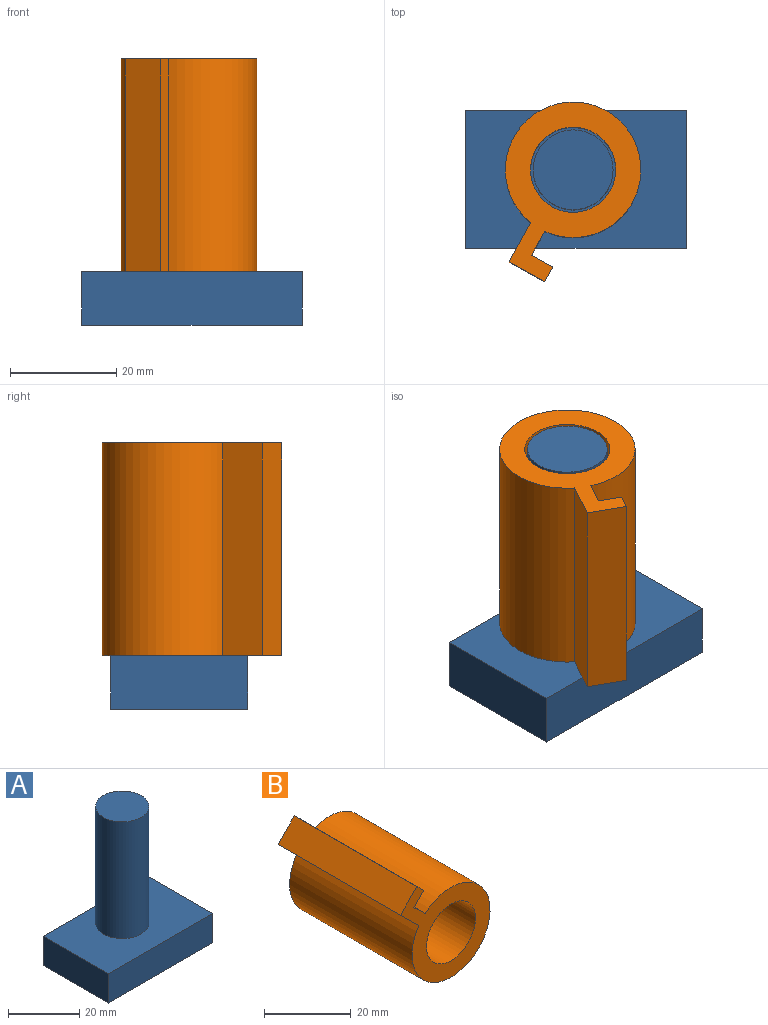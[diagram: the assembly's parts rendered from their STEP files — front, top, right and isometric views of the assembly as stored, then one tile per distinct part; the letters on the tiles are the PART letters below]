
ASSEMBLY  parts=2 mates=1
PART A: 8 faces, bbox 41.4x25.8x50 mm
  f0: cylinder r=7.5mm len=40mm, axis (0,0,-1), area 1885mm2, adj f1,f6
  f1: plane 15x15mm, normal (0,0,1), area 176.7mm2, adj f0
  f2: plane 41.36x10mm, normal (0,1,0), area 413.6mm2, adj f3,f5,f6,f7
  f3: plane 25.79x10mm, normal (-1,0,0), area 257.8mm2, adj f2,f4,f6,f7
  f4: plane 41.36x10mm, normal (0,-1,0), area 413.6mm2, adj f3,f5,f6,f7
  f5: plane 25.79x10mm, normal (1,0,0), area 257.8mm2, adj f2,f4,f6,f7
  f6: plane 41.36x25.79mm, normal (0,0,1), area 889.7mm2, adj f0,f2,f3,f4,f5
  f7: plane 41.36x25.79mm, normal (0,0,-1), area 1066.4mm2, adj f2,f3,f4,f5
PART B: 9 faces, bbox 29.3x40x31.3 mm
  f0: plane 40x6.03mm, normal (-0.7,0,-0.72), area 337.3mm2, adj f1,f5,f7,f8
  f1: cylinder r=12.73mm len=40mm, axis (0,1,0), area 3076.7mm2, adj f0,f2,f7,f8
  f2: plane 40x3.67mm, normal (0.7,0,0.72), area 205mm2, adj f1,f3,f7,f8
  f3: plane 40x3.26mm, normal (0.72,0,-0.7), area 182mm2, adj f2,f4,f7,f8
  f4: plane 40x2.26mm, normal (0.7,0,0.72), area 126.1mm2, adj f3,f5,f7,f8
  f5: plane 40x5.46mm, normal (-0.72,0,0.7), area 305.1mm2, adj f0,f4,f7,f8
  f6: cylinder r=8mm len=40mm, axis (0,1,0), area 2010.6mm2, adj f7,f8
  f7: plane 31.29x29.26mm, normal (0,-1,0), area 348.2mm2, adj f0,f1,f2,f3,f4,f5,f6
  f8: plane 31.29x29.26mm, normal (0,1,0), area 348.2mm2, adj f0,f1,f2,f3,f4,f5,f6
PLACE A t=(-24.96,-13.53,-16.34)mm fixed
PLACE B rot(axis=(0.98,0.14,0.14),91.2deg) t=(-24.96,-13.53,33.66)mm
MATE revolute A.f0 <-> B.f6  axis (0,0,1) through (-24.96,-13.53,33.66)mm
